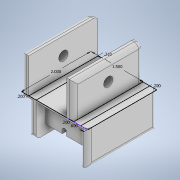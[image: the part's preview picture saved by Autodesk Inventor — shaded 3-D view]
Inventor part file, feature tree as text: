
AUTODESK INVENTOR PART (.ipt)
format: ipt  version: 2020 (Build 240168000, 168)  size: 240,128 bytes
history: native  units: in
note: dims shown in document units (in); Inventor stores cm internally (conversion verified against a paired STEP export)
features: extrude x5, sketch x3, fillet x2, hole x1
ambient origin geometry x8: Origin, YZ Plane, XZ Plane, XY Plane, X Axis, Y Axis, Z Axis, Center Point
bodies: Solid1 (feature_tree)
feature tree (11):
  extrude  "Extrusion1"  Depth=2.0in
  extrude  "Extrusion2"  Depth=0.2in
  hole  "Hole1"  [1 undecoded]
  extrude  "Extrusion3"  Depth=0.21in
  extrude  "Extrusion4"  Depth=0.6in
  extrude  "Extrusion5"  Depth=0.2in
  fillet  "Fillet1"  Radius=1.0in
  fillet  "Fillet2"  Radius=0.5906in
  sketch  "Sketch2"  dims[d0=1.5in d1=2.0in]
  sketch  "Sketch3"  dims[d2=0.2in d3=0.2in]
  sketch  "Sketch4"  dims[d4=1.0in d5=0.0in d6=0.05in d7=0.0in d8=0.5in d9=0.266in d10=0.75in d11=0.438in d12=0.25in d13=0.5635in d14=1.0in d15=0.8108in d16=0.6in d17=0.2in d18=1.0in d19=0.0in d23=0.5906in d24=1.1811in d25=0.125in d26=0.125in d27=0.7in d28=0.0in d29=0.75in d30=180.0deg d31=0.1in d32=0.125in d33=0.0in d34=0.0in d35=0.125in d36=0.125in d37=0.21in]
note: 1 required parameter value undecoded (feature->parameter linkage not recoverable at this tier; creation-order binding heuristic only, values carry confidence <= 0.55)
